# Revit family: Casement_41_D_Top_Hung_SD_Standard
name_source: partatom
category: Windows
revit_build: Autodesk Revit 2014 (Build: 20130308_1515(x64)
units: mm (PartAtom-declared; Revit-internal decimal feet)

## types (12) — shared parameters
Corrected Mullion Configuration = 2 mm  [stored 0.00656168 ft]
Custom Sash Height = 502 mm
Description = Window 41mm, Type D, Top hung, Standard sash
Frame Profile Thickness = 41 mm  [stored 0.134514 ft]
Heavy Duty Sash = No
Limit Fixed Pane Height Max = 3000 mm  [stored 9.84252 ft]
Limit Fixed Pane Height Min = 200 mm  [stored 0.656168 ft]
Limit Fixed Pane Width Max = 3000 mm  [stored 9.84252 ft]
Limit Fixed Pane Width Min = 200 mm  [stored 0.656168 ft]
Limit Sash Height Max = 1200 mm  [stored 3.93701 ft]
Limit Sash Height Min = 300 mm  [stored 0.984252 ft]
Limit Sash Width Max = 1500 mm  [stored 4.92126 ft]
Limit Sash Width Min = 300 mm  [stored 0.984252 ft]
Limit Window Width Min = 388 mm
Manufacturer = Crealco
Max System DG Unit Thickness = 25 mm  [stored 0.082021 ft]
Model = Casement 41
Rough Width = 3 mm  [stored 0.00984252 ft]
Sash Side Gap = 44 mm
Standard Mullion Different = No
Standard Sash = Yes
URL = http://www.crealco.co.za
Wall Closure = By host
zero-valued in all types: Custom Frame Offset From Exterior

## per-type parameters (varying)
| type | Clearvue Insulated LowE SHGC Value | Clearvue Insulated LowE U Value | Clearvue Insulated SHGC Value | Clearvue Insulated U Value | Clearvue SHGC Value | Clearvue U Value | Custom Windload | Custom Window Height | Custom Window Width | Energy Advantage SHGC Value | Energy Advantage U Value | Intruderprufe Insulated LowE SHGC Value | Intruderprufe Insulated LowE U Value | Intruderprufe Insulated SHGC Value | Intruderprufe Insulated U Value | Intruderprufe LowE SHGC Value | Intruderprufe LowE U Value | Intruderprufe SHGC Value | Intruderprufe U Value | Toughened Safety SHGC Value | Toughened Safety U Value |
| 41-0609T-SD-1000Pa | 0.744 | 3.8 | 0.744 | 3.88 | 0.435 | 6.2 | 1000 mm  [stored 3.28084 ft] | 890 mm  [stored 2.91995 ft] | 590 mm  [stored 1.9357 ft] | 0.393 | 5.4 | 0.618 | 2.76 | 0.618 | 2.81 | 0.366 | 5.23 | 0.41 | 6.05 | 0.435 | 6.2 |
| 41-0609T-SD-1500Pa | 0.744 | 3.8 | 0.744 | 3.88 | 0.435 | 6.2 | 1500 mm  [stored 4.92126 ft] | 890 mm  [stored 2.91995 ft] | 590 mm  [stored 1.9357 ft] | 0.393 | 5.4 | 0.618 | 2.76 | 0.618 | 2.81 | 0.366 | 5.23 | 0.41 | 6.05 | 0.435 | 6.2 |
| 41-0609T-SD-2000Pa | 0.744 | 3.8 | 0.744 | 3.88 | 0.435 | 6.2 | 2000 mm  [stored 6.56168 ft] | 890 mm  [stored 2.91995 ft] | 590 mm  [stored 1.9357 ft] | 0.393 | 5.4 | 0.618 | 2.76 | 0.618 | 2.81 | 0.366 | 5.23 | 0.41 | 6.05 | 0.435 | 6.2 |
| 41-0909T-SD-1000Pa | 0.745 | 4.09 | 0.745 | 4.17 | 0.49 | 6.16 | 1000 mm  [stored 3.28084 ft] | 890 mm  [stored 2.91995 ft] | 890 mm  [stored 2.91995 ft] | 0.442 | 5.18 | 0.619 | 2.95 | 0.619 | 3.01 | 0.412 | 5.03 | 0.462 | 6.01 | 0.49 | 6.16 |
| 41-0909T-SD-1500Pa | 0.745 | 4.09 | 0.745 | 4.17 | 0.49 | 6.16 | 1500 mm  [stored 4.92126 ft] | 890 mm  [stored 2.91995 ft] | 890 mm  [stored 2.91995 ft] | 0.442 | 5.18 | 0.619 | 2.95 | 0.619 | 3.01 | 0.412 | 5.03 | 0.462 | 6.01 | 0.49 | 6.16 |
| 41-0909T-SD-2000Pa | 0.745 | 4.09 | 0.745 | 4.17 | 0.49 | 6.16 | 2000 mm  [stored 6.56168 ft] | 890 mm  [stored 2.91995 ft] | 890 mm  [stored 2.91995 ft] | 0.442 | 5.18 | 0.619 | 2.95 | 0.619 | 3.01 | 0.412 | 5.03 | 0.462 | 6.01 | 0.49 | 6.16 |
| 41-0612T-SD-1000Pa | 0.771 | 4 | 0.771 | 4.06 | 0.499 | 6.15 | 1000 mm  [stored 3.28084 ft] | 1190 mm  [stored 3.9042 ft] | 590 mm  [stored 1.9357 ft] | 0.45 | 5.14 | 0.64 | 2.78 | 0.64 | 2.82 | 0.419 | 4.96 | 0.47 | 5.97 | 0.499 | 6.15 |
| 41-0612T-SD-1500Pa | 0.771 | 4 | 0.771 | 4.06 | 0.499 | 6.15 | 1500 mm  [stored 4.92126 ft] | 1190 mm  [stored 3.9042 ft] | 590 mm  [stored 1.9357 ft] | 0.45 | 5.14 | 0.64 | 2.78 | 0.64 | 2.82 | 0.419 | 4.96 | 0.47 | 5.97 | 0.499 | 6.15 |
| 41-0612T-SD-2000Pa | 0.771 | 4 | 0.771 | 4.06 | 0.499 | 6.15 | 2000 mm  [stored 6.56168 ft] | 1190 mm  [stored 3.9042 ft] | 590 mm  [stored 1.9357 ft] | 0.45 | 5.14 | 0.64 | 2.78 | 0.64 | 2.82 | 0.419 | 4.96 | 0.47 | 5.97 | 0.499 | 6.15 |
| 41-0912T-SD-1000Pa | 0.771 | 4.33 | 0.771 | 4.39 | 0.554 | 6.11 | 1000 mm  [stored 3.28084 ft] | 1190 mm  [stored 3.9042 ft] | 890 mm  [stored 2.91995 ft] | 0.499 | 4.92 | 0.64 | 2.99 | 0.64 | 3.04 | 0.464 | 4.76 | 0.522 | 5.94 | 0.554 | 6.11 |
| 41-0912T-SD-1500Pa | 0.771 | 4.33 | 0.771 | 4.39 | 0.554 | 6.11 | 1500 mm  [stored 4.92126 ft] | 1190 mm  [stored 3.9042 ft] | 890 mm  [stored 2.91995 ft] | 0.499 | 4.92 | 0.64 | 2.99 | 0.64 | 3.04 | 0.464 | 4.76 | 0.522 | 5.94 | 0.554 | 6.11 |
| 41-0912T-SD-2000Pa | 0.771 | 4.33 | 0.771 | 4.39 | 0.554 | 6.11 | 2000 mm  [stored 6.56168 ft] | 1190 mm  [stored 3.9042 ft] | 890 mm  [stored 2.91995 ft] | 0.499 | 4.92 | 0.64 | 2.99 | 0.64 | 3.04 | 0.464 | 4.76 | 0.522 | 5.94 | 0.554 | 6.11 |

note: [stored X ft] marks values corroborated as IEEE doubles in the binary element streams (Revit-internal decimal feet)

## geometry (parser evidence)
native form markers: Sweep x20
no freeform markers — native parametric forms only
